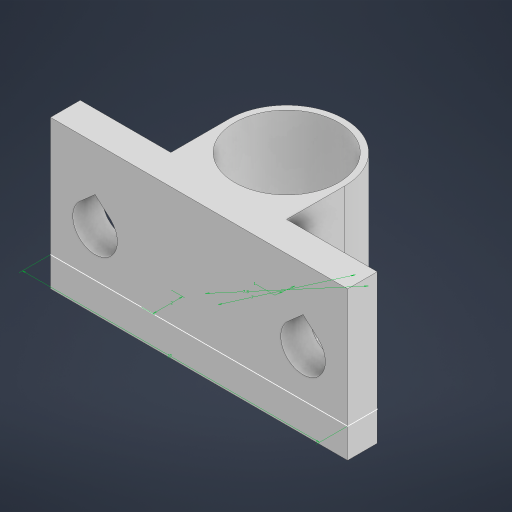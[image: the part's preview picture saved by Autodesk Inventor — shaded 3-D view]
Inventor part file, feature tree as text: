
AUTODESK INVENTOR PART (.ipt)
format: ipt  version: 2024.2 (Build 282272000, 272)  size: 353,280 bytes
history: native  units: mm
features: extrude x3, sketch x2
ambient origin geometry x8: Origin, YZ Plane, XZ Plane, XY Plane, X Axis, Y Axis, Z Axis, Center Point
bodies: Solid1 (feature_tree)
feature tree (5):
  sketch  "Sketch1"  dims[d0=7.0mm d1=7.8mm]
  extrude  "Extrusion1"  Depth=7.8mm
  extrude  "Extrusion2"  Depth=8.0mm TaperAngle=0.0deg
  extrude  "Extrusion3"  Depth=2.0mm TaperAngle=0.0deg
  sketch  "Sketch2"  dims[d2=1.0mm d3=8.0mm d4=0.0mm d5=2.0mm d6=0.0mm d7=2.0mm d10=20.0mm d11=3.0mm d12=3.0mm d13=3.0mm d14=3.0mm d15=5.0mm d16=0.0mm d17=0.0mm d18=0.5mm d19=0.5mm]
